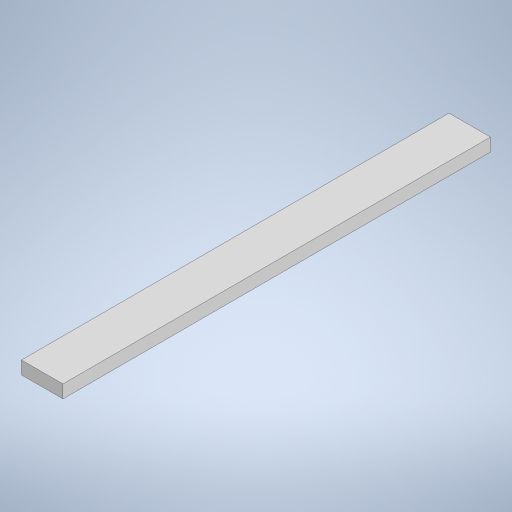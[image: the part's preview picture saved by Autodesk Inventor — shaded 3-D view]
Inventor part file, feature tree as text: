
AUTODESK INVENTOR PART (.ipt)
format: ipt  version: 2024 (Build 280153000, 153)  size: 529,920 bytes
history: native  units: mm
features: extrude x1, sketch x1
ambient origin geometry x8: Origin, YZ Plane, XZ Plane, XY Plane, X Axis, Y Axis, Z Axis, Center Point
bodies: Solid1 (feature_tree)
feature tree (2):
  extrude  "Extrusion1"  Depth=103.0mm
  sketch  "Sketch1"  dims[d0=10.0mm d1=103.0mm d2=3.125mm d3=0.0mm]
